# Revit family: FU_Table_Sandler_Plania Retangular Tops
name_source: partatom
category: Furniture
units: mm (PartAtom-declared; Revit-internal decimal feet)

## family parameters
Always vertical = Yes
Cut with Voids When Loaded = No
OmniClass Number = 23.40.20.00
OmniClass Title = General Furniture and Specialties
Room Calculation Point = No
Shared = No
Work Plane-Based = No

## types (34) — shared parameters
Base Height = 43 mm  [stored 0.141076 ft]
Manufacturer = Sandler
URL = https://www.sandlerseating.com
zero-valued in all types: Default Elevation

## per-type parameters (varying)
| type | Base Frame Finish | Depth | Description | Height | Model | Top | Top Finish | Top Thickness | Width |
| PL50018 - Wood - 36x71inch - 90x180cm | Epoxy - M2_G42 | 900 mm  [stored 2.95276 ft] | 90cm x 180cm / 36″ x 71″ Laminated or Lacquered Rectangular table top with standard epoxy painted structural frame. | 65 mm  [stored 0.213255 ft] | PL50018 - Wood | PL_Rect_Wood : Planina Wooden Top | Wood - Oak - Natural - V | 22 mm  [stored 0.0721785 ft] | 1800 mm  [stored 5.90551 ft] |
| PL50020 - Wood - 36x79inch - 90x200cm | Epoxy - M2_M56 | 900 mm  [stored 2.95276 ft] | 90cm x 200cm / 36″ x 79″ Laminated or Lacquered Rectangular table top with standard epoxy painted structural frame. | 65 mm  [stored 0.213255 ft] | PL50020 - Wood | PL_Rect_Wood : Planina Wooden Top | Wood - Oak - Walnut | 22 mm  [stored 0.0721785 ft] | 2000 mm  [stored 6.56168 ft] |
| PL50018 - HPL/Fenix - 36x71inch - 90x180cm | Epoxy - M1_B00 - Black | 900 mm  [stored 2.95276 ft] | 90cm x 180cm / 36″ x 71″ HPL or Fenix Rectangular table top with standard epoxy painted structural frame. | 55 mm  [stored 0.180446 ft] | PL50018 - HPL/Fenix | PL_Rect_HPL : Plania HPL/Fenix Top | HPL - Solid - White | 12 mm  [stored 0.0393701 ft] | 1800 mm  [stored 5.90551 ft] |
| PL50020 - HPL/Fenix - 36x79inch - 90x200cm | Epoxy - M1_Aluminum | 900 mm  [stored 2.95276 ft] | 90cm x 200cm / 36″ x 79″ HPL or Fenix Rectangular table top with standard epoxy painted structural frame. | 55 mm  [stored 0.180446 ft] | PL50020 - HPL/Fenix | PL_Rect_HPL : Plania HPL/Fenix Top | HPL - Solid - White | 12 mm  [stored 0.0393701 ft] | 2000 mm  [stored 6.56168 ft] |
| PL50024 - Wood - 36x95inch - 90x240cm | Epoxy - M2_M56 | 900 mm  [stored 2.95276 ft] | 90cm x 240cm / 36″ x 95″ Laminated or Lacquered Rectangular table top with standard epoxy painted structural frame. | 65 mm  [stored 0.213255 ft] | PL50024 - Wood | PL_Rect_Wood : Planina Wooden Top | Wood - Oak - Walnut | 22 mm  [stored 0.0721785 ft] | 2400 mm  [stored 7.87402 ft] |
| PL50024 - HPL/Fenix - 36x95inch - 90x240cm | Epoxy - M2_G42 | 900 mm  [stored 2.95276 ft] | 90cm x 240cm / 36″ x 95″ HPL or Fenix Rectangular table top with standard epoxy painted structural frame. | 55 mm  [stored 0.180446 ft] | PL50024 - HPL/Fenix | PL_Rect_HPL : Plania HPL/Fenix Top | HPL - Solid - Black | 12 mm  [stored 0.0393701 ft] | 2400 mm  [stored 7.87402 ft] |
| PL50028 - HPL/Fenix - 36x110inch - 90x280cm | Epoxy - M2 - Rust Brown | 900 mm  [stored 2.95276 ft] | 90cm x 280cm / 36″ x 110″ HPL or Fenix Rectangular table top with standard epoxy painted structural frame. | 55 mm  [stored 0.180446 ft] | PL50028 - HPL/Fenix | PL_Rect_HPL : Plania HPL/Fenix Top | HPL - Solid - White | 12 mm  [stored 0.0393701 ft] | 2800 mm  [stored 9.18635 ft] |
| PL50028 - Wood - 36x110inch - 90x280cm | Epoxy - M2_M56 | 900 mm  [stored 2.95276 ft] | 90cm x 280cm / 36″ x 110″ Laminated or Lacquered Rectangular table top with standard epoxy painted structural frame. | 65 mm  [stored 0.213255 ft] | PL50028 - Wood | PL_Rect_Wood : Planina Wooden Top | Wood - Oak - Walnut | 22 mm  [stored 0.0721785 ft] | 2800 mm  [stored 9.18635 ft] |
| PL50032 - Wood - 36x126inch - 90x320cm | Epoxy - M2_M56 | 900 mm  [stored 2.95276 ft] | 90cm x 320cm / 36″ x 126″ Laminated or Lacquered Rectangular table top with standard epoxy painted structural frame. | 65 mm  [stored 0.213255 ft] | PL50032 - Wood | PL_Rect_Wood : Planina Wooden Top | Solid Walnut | 22 mm  [stored 0.0721785 ft] | 3200 mm  [stored 10.4987 ft] |
| PL50032 - HPL/Fenix - 36x126inch - 90x320cm | Epoxy - M2_M56 | 900 mm  [stored 2.95276 ft] | 90cm x 320cm / 36″ x 126″ HPL or Fenix Rectangular table top with standard epoxy painted structural frame. | 55 mm  [stored 0.180446 ft] | PL50032 - HPL/Fenix | PL_Rect_HPL : Plania HPL/Fenix Top | Lacquer - W1 - B00 Black | 12 mm  [stored 0.0393701 ft] | 3200 mm  [stored 10.4987 ft] |
| PL50040 - Wood - 36x158inch - 90x400cm | Epoxy - M2_V16 | 900 mm  [stored 2.95276 ft] | 90cm x 400cm / 36″ x 158″ Laminated or Lacquered Rectangular table top with standard epoxy painted structural frame. | 65 mm  [stored 0.213255 ft] | PL50040 - Wood | PL_Rect_Wood : Planina Wooden Top | Lacquer - W2 - Y62 | 22 mm  [stored 0.0721785 ft] | 4000 mm  [stored 13.1234 ft] |
| PL50040 - HPL/Fenix - 36x158inch - 90x400cm | Epoxy - M2_V16 | 900 mm  [stored 2.95276 ft] | 90cm x 400cm / 36″ x 158″ HPL or Fenix Rectangular table top with standard epoxy painted structural frame. | 55 mm  [stored 0.180446 ft] | PL50040 - HPL/Fenix | PL_Rect_HPL : Plania HPL/Fenix Top | HPL - Solid - White | 12 mm  [stored 0.0393701 ft] | 4000 mm  [stored 13.1234 ft] |
| PL50056 - Wood - 36x220inch - 90x560cm | Epoxy - M2_M56 | 900 mm  [stored 2.95276 ft] | 90cm x 560cm / 36″ x 220″ Laminated or Lacquered Rectangular table top with standard epoxy painted structural frame. | 65 mm  [stored 0.213255 ft] | PL50056 - Wood | PL_Rect_Wood : Planina Wooden Top | Lacquer - W2 - M82 | 22 mm  [stored 0.0721785 ft] | 5600 mm  [stored 18.3727 ft] |
| PL50056 - HPL/Fenix - 36x220inch - 90x560cm | Epoxy - M2_M56 | 900 mm  [stored 2.95276 ft] | 90cm x 560cm / 36″ x 220″ HPL or Fenix Rectangular table top with standard epoxy painted structural frame. | 55 mm  [stored 0.180446 ft] | PL50056 - HPL/Fenix | PL_Rect_HPL : Plania HPL/Fenix Top | HPL - Solid - White | 12 mm  [stored 0.0393701 ft] | 5600 mm  [stored 18.3727 ft] |
| PL50072 - HPL/Fenix - 36x283inch - 90x720cm | Lacquer - W1 - B00 Black | 900 mm  [stored 2.95276 ft] | 90cm x 720cm / 36″ x 283″ HPL or Fenix Rectangular table top with standard epoxy painted structural frame. | 55 mm  [stored 0.180446 ft] | PL50072 - HPL/Fenix | PL_Rect_HPL : Plania HPL/Fenix Top | HPL - Solid - White | 12 mm  [stored 0.0393701 ft] | 7200 mm  [stored 23.622 ft] |
| PL50072 - Wood - 36x283inch - 90x720cm | Epoxy - M1_B00 - Black | 900 mm  [stored 2.95276 ft] | 90cm x 720cm / 36″ x 283″ Laminated or Lacquered Rectangular table top with standard epoxy painted structural frame. | 65 mm  [stored 0.213255 ft] | PL50072 - Wood | PL_Rect_Wood : Planina Wooden Top | Lacquer - W2 - M82 | 22 mm  [stored 0.0721785 ft] | 7200 mm  [stored 23.622 ft] |
| PL50088 - Wood - 36x346inch - 90x880cm | Epoxy - M2_Y62 | 900 mm  [stored 2.95276 ft] | 90cm x 880cm / 36″ x 346″ Laminated or Lacquered Rectangular table top with standard epoxy painted structural frame. | 65 mm  [stored 0.213255 ft] | PL50088 - Wood | PL_Rect_Wood : Planina Wooden Top | Lacquer - W2 - G49 | 22 mm  [stored 0.0721785 ft] | 8800 mm |
| PL50088 - HPL/Fenix - 36x346inch - 90x880cm | Epoxy - M2_G42 | 900 mm  [stored 2.95276 ft] | 90cm x 880cm / 36″ x 346″ HPL or Fenix Rectangular table top with standard epoxy painted structural frame. | 55 mm  [stored 0.180446 ft] | PL50088 - HPL/Fenix | PL_Rect_HPL : Plania HPL/Fenix Top | HPL - Solid - White | 12 mm  [stored 0.0393701 ft] | 8800 mm |
| PL50120 - HPL/Fenix - 48x79inch - 120x200cm | Epoxy - M2 - Rust Grey | 1200 mm | 120cm x 200cm / 48″ x 79″ HPL or Fenix Rectangular table top with standard epoxy painted structural frame. | 55 mm  [stored 0.180446 ft] | PL50120 - HPL/Fenix | PL_Rect_HPL : Plania HPL/Fenix Top | HPL - Solid - White | 12 mm  [stored 0.0393701 ft] | 2000 mm  [stored 6.56168 ft] |
| PL50120 - Wood - 48x79inch - 120x200cm | Epoxy - M2 - Rust Brown | 1200 mm | 120cm x 200cm / 48″ x 79″ Laminated or Lacquered Rectangular table top with standard epoxy painted structural frame. | 65 mm  [stored 0.213255 ft] | PL50120 - Wood | PL_Rect_Wood : Planina Wooden Top | Lacquer - W2 - B36 | 22 mm  [stored 0.0721785 ft] | 2000 mm  [stored 6.56168 ft] |
| PL50124 - Wood - 48x95inch - 120x240cm | Epoxy - M2 - Rust Brown | 1200 mm | 120cm x 240cm / 48″ x 95″ Laminated or Lacquered Rectangular table top with standard epoxy painted structural frame. | 65 mm  [stored 0.213255 ft] | PL50124 - Wood | PL_Rect_Wood : Planina Wooden Top | Wood - Oak - Walnut | 22 mm  [stored 0.0721785 ft] | 2400 mm  [stored 7.87402 ft] |
| PL50124 - HPL/Fenix - 48x95inch - 120x240cm | Epoxy - M1_Aluminum | 1200 mm | 120cm x 240cm / 48″ x 95″ HPL or Fenix Rectangular table top with standard epoxy painted structural frame. | 55 mm  [stored 0.180446 ft] | PL50124 - HPL/Fenix | PL_Rect_HPL : Plania HPL/Fenix Top | HPL - Solid - Black | 12 mm  [stored 0.0393701 ft] | 2400 mm  [stored 7.87402 ft] |
| PL50128 - Wood - 48x110inch - 120x280cm | Epoxy - M2_B40 | 1200 mm | 120cm x 280cm / 48″ x 110″ Laminated or Lacquered Rectangular table top with standard epoxy painted structural frame. | 65 mm  [stored 0.213255 ft] | PL50128 - Wood | PL_Rect_Wood : Planina Wooden Top | Wood - Oak - Natural - V | 22 mm  [stored 0.0721785 ft] | 2800 mm  [stored 9.18635 ft] |
| PL50128 - HPL/Fenix - 48x110inch - 120x280cm | Epoxy - M2_B40 | 1200 mm | 120cm x 280cm / 48″ x 110″ HPL or Fenix Rectangular table top with standard epoxy painted structural frame. | 55 mm  [stored 0.180446 ft] | PL50128 - HPL/Fenix | PL_Rect_HPL : Plania HPL/Fenix Top | HPL - Solid - White | 12 mm  [stored 0.0393701 ft] | 2800 mm  [stored 9.18635 ft] |
| PL50132 - HPL/Fenix - 48x126inch - 120x320cm | Epoxy - M2_G42 | 1200 mm | 120cm x 320cm / 48″ x 126″ HPL or Fenix Rectangular table top with standard epoxy painted structural frame. | 55 mm  [stored 0.180446 ft] | PL50132 - HPL/Fenix | PL_Rect_HPL : Plania HPL/Fenix Top | HPL - Solid - White | 12 mm  [stored 0.0393701 ft] | 3200 mm  [stored 10.4987 ft] |
| PL50132 - Wood - 48x126inch - 120x320cm | Epoxy - M2_P70 | 1200 mm | 120cm x 320cm / 48″ x 126″ HPL or Fenix Rectangular table top with standard epoxy painted structural frame. | 65 mm  [stored 0.213255 ft] | PL50132 - Wood | PL_Rect_Wood : Planina Wooden Top | Lacquer - W2 - P70 | 22 mm  [stored 0.0721785 ft] | 3200 mm  [stored 10.4987 ft] |
| PL50140 - Wood - 48x158inch - 120x400cm | Epoxy - M2_M38 | 1200 mm | 120cm x 400cm / 48″ x 158″ Laminated or Lacquered Rectangular table top with standard epoxy painted structural frame. | 65 mm  [stored 0.213255 ft] | PL50140 - Wood | PL_Rect_Wood : Planina Wooden Top | Lacquer - W2 - G42 | 22 mm  [stored 0.0721785 ft] | 4000 mm  [stored 13.1234 ft] |
| PL50140 - HPL/Fenix - 48x158inch - 120x400cm | Epoxy - M2_G42 | 1200 mm | 120cm x 400cm / 48″ x 158″ HPL or Fenix Rectangular table top with standard epoxy painted structural frame. | 55 mm  [stored 0.180446 ft] | PL50140 - HPL/Fenix | PL_Rect_HPL : Plania HPL/Fenix Top | HPL - Solid - White | 12 mm  [stored 0.0393701 ft] | 4000 mm  [stored 13.1234 ft] |
| PL50156 - HPL/Fenix - 48x220inch - 120x560cm | Epoxy - M2_G49 | 1200 mm | 120cm x 560cm / 48″ x 220″ HPL or Fenix Rectangular table top with standard epoxy painted structural frame. | 55 mm  [stored 0.180446 ft] | PL50156 - HPL/Fenix | PL_Rect_HPL : Plania HPL/Fenix Top | HPL - Solid - White | 12 mm  [stored 0.0393701 ft] | 5600 mm  [stored 18.3727 ft] |
| PL50156 - Wood - 48x220inch - 120x560cm | Epoxy - M2_B36 | 1200 mm | 120cm x 560cm / 48″ x 220″ Laminated or Lacquered Rectangular table top with standard epoxy painted structural frame. | 65 mm  [stored 0.213255 ft] | PL50156 - Wood | PL_Rect_Wood : Planina Wooden Top | Lacquer - W2 - V74 | 22 mm  [stored 0.0721785 ft] | 5600 mm  [stored 18.3727 ft] |
| PL50172 - Wood - 48x283inch - 120x720cm | Epoxy - M2_B44 | 1200 mm | 120cm x 720cm / 48″ x 283″ Laminated or Lacquered Rectangular table top with standard epoxy painted structural frame. | 65 mm  [stored 0.213255 ft] | PL50172 - Wood | PL_Rect_Wood : Planina Wooden Top | Lacquer - W2 - M56 | 22 mm  [stored 0.0721785 ft] | 7200 mm  [stored 23.622 ft] |
| PL50172 - HPL/Fenix - 48x283inch - 120x720cm | Epoxy - M2_M82 | 1200 mm | 120cm x 720cm / 48″ x 283″ HPL or Fenix Rectangular table top with standard epoxy painted structural frame. | 55 mm  [stored 0.180446 ft] | PL50172 - HPL/Fenix | PL_Rect_HPL : Plania HPL/Fenix Top | Lacquer - W1 - B00 Black | 12 mm  [stored 0.0393701 ft] | 7200 mm  [stored 23.622 ft] |
| PL50188 - HPL/Fenix - 48x346inch - 120x880cm | Epoxy - M2_B44 | 1200 mm | 120cm x 880cm / 48″ x 346″ HPL or Fenix Rectangular table top with standard epoxy painted structural frame. | 55 mm  [stored 0.180446 ft] | PL50188 - HPL/Fenix | PL_Rect_HPL : Plania HPL/Fenix Top | Lacquer - W1 - B00 Black | 12 mm  [stored 0.0393701 ft] | 8800 mm |
| PL50188 - Wood - 48x346inch - 120x880cm | Epoxy - M1_W01 - White | 1200 mm | 120cm x 880cm / 48″ x 346″ Laminated or Lacquered Rectangular table top with standard epoxy painted structural frame. | 65 mm  [stored 0.213255 ft] | PL50188 - Wood | PL_Rect_Wood : Planina Wooden Top | Lacquer - W1 - W01 White | 22 mm  [stored 0.0721785 ft] | 8800 mm |

note: [stored X ft] marks values corroborated as IEEE doubles in the binary element streams (Revit-internal decimal feet)

## geometry (parser evidence)
native form markers: Sweep x11
no freeform markers — native parametric forms only
